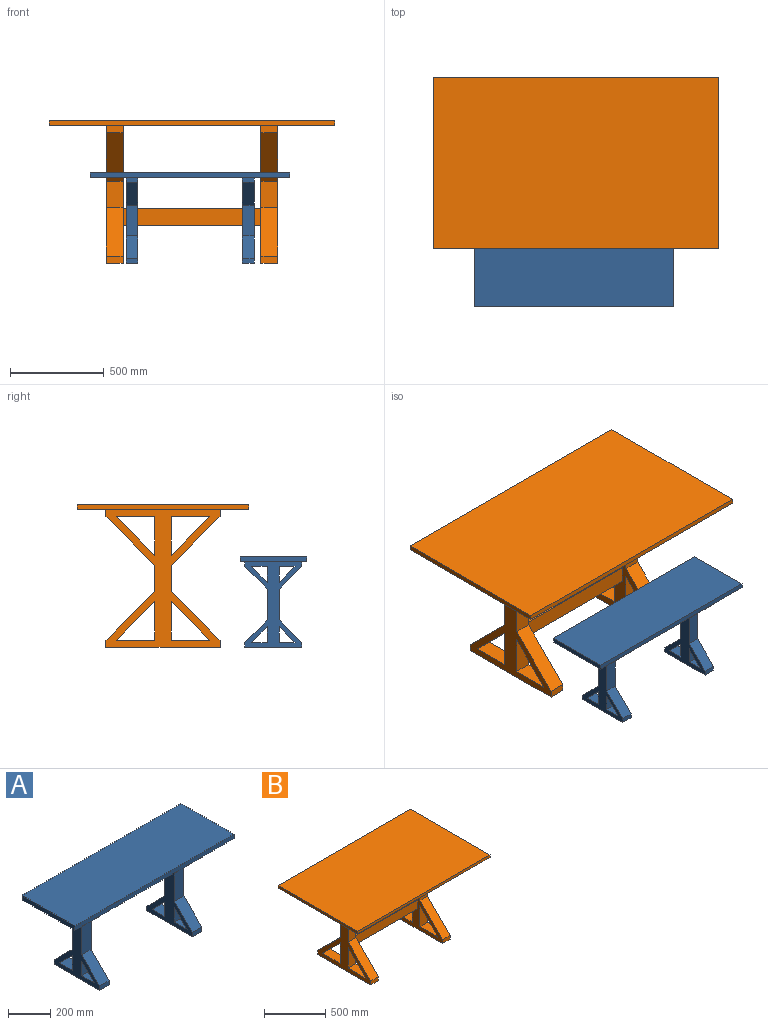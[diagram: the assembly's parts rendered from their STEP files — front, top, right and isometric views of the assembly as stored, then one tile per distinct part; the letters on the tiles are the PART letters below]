
ASSEMBLY  parts=2 mates=1
PART A: 56 faces, bbox 1066.8x355.6x482.6 mm
  f0: plane 165.1x63.5mm, normal (0,-1,0), area 10483.8mm2, adj f23,f25,f53,f55
  f1: plane 84.73x63.5mm, normal (0,0,1), area 5380.3mm2, adj f23,f25,f32,f54
  f2: plane 84.73x63.5mm, normal (0,0,-1), area 5380.3mm2, adj f3,f23,f25,f52
  f3: plane 84.73x63.5mm, normal (0,-1,0), area 5380.3mm2, adj f2,f23,f25,f52
  f4: plane 165.1x63.5mm, normal (0,1,0), area 10483.8mm2, adj f23,f25,f48,f51
  f5: plane 84.73x63.5mm, normal (0,1,0), area 5380.3mm2, adj f23,f25,f27,f49
  f6: plane 84.73x63.5mm, normal (0,-1,0), area 5380.3mm2, adj f7,f20,f22,f46
  f7: plane 84.73x63.5mm, normal (0,0,1), area 5380.3mm2, adj f6,f20,f22,f46
  f8: plane 84.73x63.5mm, normal (0,0,-1), area 5380.3mm2, adj f20,f22,f30,f44
  f9: plane 165.1x63.5mm, normal (0,-1,0), area 10483.8mm2, adj f20,f22,f45,f47
  f10: plane 84.73x63.5mm, normal (0,1,0), area 5380.3mm2, adj f20,f22,f35,f42
  f11: plane 165.1x63.5mm, normal (0,1,0), area 10483.8mm2, adj f20,f22,f41,f43
  f12: plane 84.73x63.5mm, normal (0,0,-1), area 5380.3mm2, adj f20,f22,f29,f40
  f13: plane 1066.8x355.6mm, normal (0,0,-1), area 340644.5mm2, adj f14,f15,f16,f17,f19,f20,f21,f22
  f14: plane 355.6x25.4mm, normal (-1,0,0), area 9032.2mm2, adj f13,f15,f17,f18
  f15: plane 1066.8x25.4mm, normal (0,1,0), area 27096.7mm2, adj f13,f14,f16,f18
  f16: plane 355.6x25.4mm, normal (1,0,0), area 9032.2mm2, adj f13,f15,f17,f18
  f17: plane 1066.8x25.4mm, normal (0,-1,0), area 27096.7mm2, adj f13,f14,f16,f18
  f18: plane 1066.8x355.6mm, normal (0,0,1), area 379354.1mm2, adj f14,f15,f16,f17
  f19: plane 63.5x25.4mm, normal (0,-1,0), area 1612.9mm2, adj f13,f20,f22,f45
  f20: plane 457.2x304.8mm, normal (-1,0,0), area 56045.1mm2, adj f6,f7,f8,f9,f10,f11,f12,f13
  f21: plane 63.5x25.4mm, normal (0,1,0), area 1612.9mm2, adj f13,f20,f22,f41
  f22: plane 457.2x304.8mm, normal (1,0,0), area 56045.1mm2, adj f6,f7,f8,f9,f10,f11,f12,f13
  f23: plane 457.2x304.8mm, normal (-1,0,0), area 56045.1mm2, adj f0,f1,f2,f3,f4,f5,f13,f24
  f24: plane 63.5x25.4mm, normal (0,1,0), area 1612.9mm2, adj f13,f23,f25,f48
  f25: plane 457.2x304.8mm, normal (1,0,0), area 56045.1mm2, adj f0,f1,f2,f3,f4,f5,f13,f24
  f26: plane 63.5x25.4mm, normal (0,-1,0), area 1612.9mm2, adj f13,f23,f25,f53
  f27: plane 84.73x63.5mm, normal (0,0,-1), area 5380.3mm2, adj f5,f23,f25,f49
  f28: plane 304.8x63.5mm, normal (0,0,-1), area 19354.8mm2, adj f20,f22,f34,f36
  f29: plane 84.73x63.5mm, normal (0,1,0), area 5380.3mm2, adj f12,f20,f22,f40
  f30: plane 84.73x63.5mm, normal (0,-1,0), area 5380.3mm2, adj f8,f20,f22,f44
  f31: plane 304.8x63.5mm, normal (0,0,-1), area 19354.8mm2, adj f23,f25,f37,f38
  f32: plane 84.73x63.5mm, normal (0,-1,0), area 5380.3mm2, adj f1,f23,f25,f54
  f33: plane 84.73x63.5mm, normal (0,1,0), area 5380.3mm2, adj f23,f25,f39,f50
  f34: plane 63.5x25.4mm, normal (0,1,0), area 1612.9mm2, adj f20,f22,f28,f43
  f35: plane 84.73x63.5mm, normal (0,0,1), area 5380.3mm2, adj f10,f20,f22,f42
  f36: plane 63.5x25.4mm, normal (0,-1,0), area 1612.9mm2, adj f20,f22,f28,f47
  f37: plane 63.5x25.4mm, normal (0,-1,0), area 1612.9mm2, adj f23,f25,f31,f55
  f38: plane 63.5x25.4mm, normal (0,1,0), area 1612.9mm2, adj f23,f25,f31,f51
  f39: plane 84.73x63.5mm, normal (0,0,1), area 5380.3mm2, adj f23,f25,f33,f50
  f40: plane 84.73x84.73mm, normal (0,-0.71,0.71), area 7608.9mm2, adj f12,f20,f22,f29
  f41: plane 120.65x120.65mm, normal (0,0.71,-0.71), area 10834.7mm2, adj f11,f20,f21,f22
  f42: plane 84.73x84.73mm, normal (0,-0.71,-0.71), area 7608.9mm2, adj f10,f20,f22,f35
  f43: plane 120.65x120.65mm, normal (0,0.71,0.71), area 10834.7mm2, adj f11,f20,f22,f34
  f44: plane 84.73x84.73mm, normal (0,0.71,0.71), area 7608.9mm2, adj f8,f20,f22,f30
  f45: plane 120.65x120.65mm, normal (0,-0.71,-0.71), area 10834.7mm2, adj f9,f19,f20,f22
  f46: plane 84.73x84.73mm, normal (0,0.71,-0.71), area 7608.9mm2, adj f6,f7,f20,f22
  f47: plane 120.65x120.65mm, normal (0,-0.71,0.71), area 10834.7mm2, adj f9,f20,f22,f36
  f48: plane 120.65x120.65mm, normal (0,0.71,-0.71), area 10834.7mm2, adj f4,f23,f24,f25
  f49: plane 84.73x84.73mm, normal (0,-0.71,0.71), area 7608.9mm2, adj f5,f23,f25,f27
  f50: plane 84.73x84.73mm, normal (0,-0.71,-0.71), area 7608.9mm2, adj f23,f25,f33,f39
  f51: plane 120.65x120.65mm, normal (0,0.71,0.71), area 10834.7mm2, adj f4,f23,f25,f38
  f52: plane 84.73x84.73mm, normal (0,0.71,0.71), area 7608.9mm2, adj f2,f3,f23,f25
  f53: plane 120.65x120.65mm, normal (0,-0.71,-0.71), area 10834.7mm2, adj f0,f23,f25,f26
  f54: plane 84.73x84.73mm, normal (0,0.71,-0.71), area 7608.9mm2, adj f1,f23,f25,f32
  f55: plane 120.65x120.65mm, normal (0,-0.71,0.71), area 10834.7mm2, adj f0,f23,f25,f37
PART B: 60 faces, bbox 1524x914.4x762 mm
  f0: plane 139.7x88.9mm, normal (0,-1,0), area 12419.3mm2, adj f13,f29,f57,f58
  f1: plane 206.47x88.9mm, normal (0,-1,0), area 18355mm2, adj f13,f18,f29,f56
  f2: plane 139.7x88.9mm, normal (0,1,0), area 12419.3mm2, adj f13,f29,f52,f55
  f3: plane 206.47x88.9mm, normal (0,0,1), area 18355mm2, adj f13,f15,f29,f54
  f4: plane 206.47x88.9mm, normal (0,1,0), area 18355mm2, adj f5,f13,f29,f53
  f5: plane 206.47x88.9mm, normal (0,0,-1), area 18355mm2, adj f4,f13,f29,f53
  f6: plane 206.47x88.9mm, normal (0,-1,0), area 18355mm2, adj f12,f27,f36,f51
  f7: plane 139.7x88.9mm, normal (0,-1,0), area 12419.3mm2, adj f12,f27,f49,f50
  f8: plane 206.47x88.9mm, normal (0,1,0), area 18355mm2, adj f9,f12,f27,f46
  f9: plane 206.47x88.9mm, normal (0,0,1), area 18355mm2, adj f8,f12,f27,f46
  f10: plane 139.7x88.9mm, normal (0,1,0), area 12419.3mm2, adj f12,f27,f45,f47
  f11: plane 206.47x88.9mm, normal (0,0,-1), area 18355mm2, adj f12,f17,f27,f44
  f12: plane 736.6x609.6mm, normal (1,0,0), area 152079.8mm2, adj f6,f7,f8,f9,f10,f11,f16,f17
  f13: plane 736.6x609.6mm, normal (-1,0,0), area 152079.8mm2, adj f0,f1,f2,f3,f4,f5,f14,f15
  f14: plane 206.47x88.9mm, normal (0,-1,0), area 18355mm2, adj f13,f29,f39,f59
  f15: plane 206.47x88.9mm, normal (0,1,0), area 18355mm2, adj f3,f13,f29,f54
  f16: plane 206.47x88.9mm, normal (0,-1,0), area 18355mm2, adj f12,f27,f28,f48
  f17: plane 206.47x88.9mm, normal (0,1,0), area 18355mm2, adj f11,f12,f27,f44
  f18: plane 206.47x88.9mm, normal (0,0,-1), area 18355mm2, adj f1,f13,f29,f56
  f19: plane 1524x914.4mm, normal (0,0,-1), area 1285158.7mm2, adj f12,f13,f20,f21,f22,f23,f25,f26
  f20: plane 1524x25.4mm, normal (0,1,0), area 38709.6mm2, adj f19,f21,f23,f24
  f21: plane 914.4x25.4mm, normal (-1,0,0), area 23225.8mm2, adj f19,f20,f22,f24
  f22: plane 1524x25.4mm, normal (0,-1,0), area 38709.6mm2, adj f19,f21,f23,f24
  f23: plane 914.4x25.4mm, normal (1,0,0), area 23225.8mm2, adj f19,f20,f22,f24
  f24: plane 1524x914.4mm, normal (0,0,1), area 1393545.6mm2, adj f20,f21,f22,f23
  f25: plane 88.9x38.1mm, normal (0,-1,0), area 3387.1mm2, adj f12,f19,f27,f49
  f26: plane 88.9x38.1mm, normal (0,1,0), area 3387.1mm2, adj f12,f19,f27,f45
  f27: plane 736.6x609.6mm, normal (-1,0,0), area 155466.9mm2, adj f6,f7,f8,f9,f10,f11,f16,f17
  f28: plane 206.47x88.9mm, normal (0,0,-1), area 18355mm2, adj f12,f16,f27,f48
  f29: plane 736.6x609.6mm, normal (1,0,0), area 155466.9mm2, adj f0,f1,f2,f3,f4,f5,f14,f15
  f30: plane 88.9x38.1mm, normal (0,1,0), area 3387.1mm2, adj f13,f19,f29,f52
  f31: plane 88.9x38.1mm, normal (0,-1,0), area 3387.1mm2, adj f13,f19,f29,f57
  f32: plane 609.6x88.9mm, normal (0,0,-1), area 54193.4mm2, adj f12,f27,f34,f35
  f33: plane 609.6x88.9mm, normal (0,0,-1), area 54193.4mm2, adj f13,f29,f37,f38
  f34: plane 88.9x38.1mm, normal (0,1,0), area 3387.1mm2, adj f12,f27,f32,f47
  f35: plane 88.9x38.1mm, normal (0,-1,0), area 3387.1mm2, adj f12,f27,f32,f50
  f36: plane 206.47x88.9mm, normal (0,0,1), area 18355mm2, adj f6,f12,f27,f51
  f37: plane 88.9x38.1mm, normal (0,1,0), area 3387.1mm2, adj f13,f29,f33,f55
  f38: plane 88.9x38.1mm, normal (0,-1,0), area 3387.1mm2, adj f13,f29,f33,f58
  f39: plane 206.47x88.9mm, normal (0,0,1), area 18355mm2, adj f13,f14,f29,f59
  f40: plane 736.6x38.1mm, normal (0,0,-1), area 28064.5mm2, adj f12,f13,f41,f42
  f41: plane 736.6x88.9mm, normal (0,-1,0), area 65483.7mm2, adj f12,f13,f40,f43
  f42: plane 736.6x88.9mm, normal (0,1,0), area 65483.7mm2, adj f12,f13,f40,f43
  f43: plane 736.6x38.1mm, normal (0,0,1), area 28064.5mm2, adj f12,f13,f41,f42
  f44: plane 206.47x206.47mm, normal (0,-0.71,0.71), area 25958mm2, adj f11,f12,f17,f27
  f45: plane 260.35x260.35mm, normal (0,0.71,-0.71), area 32732.1mm2, adj f10,f12,f26,f27
  f46: plane 206.47x206.47mm, normal (0,-0.71,-0.71), area 25958mm2, adj f8,f9,f12,f27
  f47: plane 260.35x260.35mm, normal (0,0.71,0.71), area 32732.1mm2, adj f10,f12,f27,f34
  f48: plane 206.47x206.47mm, normal (0,0.71,0.71), area 25958mm2, adj f12,f16,f27,f28
  f49: plane 260.35x260.35mm, normal (0,-0.71,-0.71), area 32732.1mm2, adj f7,f12,f25,f27
  f50: plane 260.35x260.35mm, normal (0,-0.71,0.71), area 32732.1mm2, adj f7,f12,f27,f35
  f51: plane 206.47x206.47mm, normal (0,0.71,-0.71), area 25958mm2, adj f6,f12,f27,f36
  f52: plane 260.35x260.35mm, normal (0,0.71,-0.71), area 32732.1mm2, adj f2,f13,f29,f30
  f53: plane 206.47x206.47mm, normal (0,-0.71,0.71), area 25958mm2, adj f4,f5,f13,f29
  f54: plane 206.47x206.47mm, normal (0,-0.71,-0.71), area 25958mm2, adj f3,f13,f15,f29
  f55: plane 260.35x260.35mm, normal (0,0.71,0.71), area 32732.1mm2, adj f2,f13,f29,f37
  f56: plane 206.47x206.47mm, normal (0,0.71,0.71), area 25958mm2, adj f1,f13,f18,f29
  f57: plane 260.35x260.35mm, normal (0,-0.71,-0.71), area 32732.1mm2, adj f0,f13,f29,f31
  f58: plane 260.35x260.35mm, normal (0,-0.71,0.71), area 32732.1mm2, adj f0,f13,f29,f38
  f59: plane 206.47x206.47mm, normal (0,0.71,-0.71), area 25958mm2, adj f13,f14,f29,f39
PLACE A t=(-313.19,38.7,-426.19)mm
PLACE B t=(-303.51,-184.09,-426.19)mm fixed
MATE planar A.f28 <-> B.f32  axis (0,0,-1) through (-624.34,-773.57,-1162.79)mm
